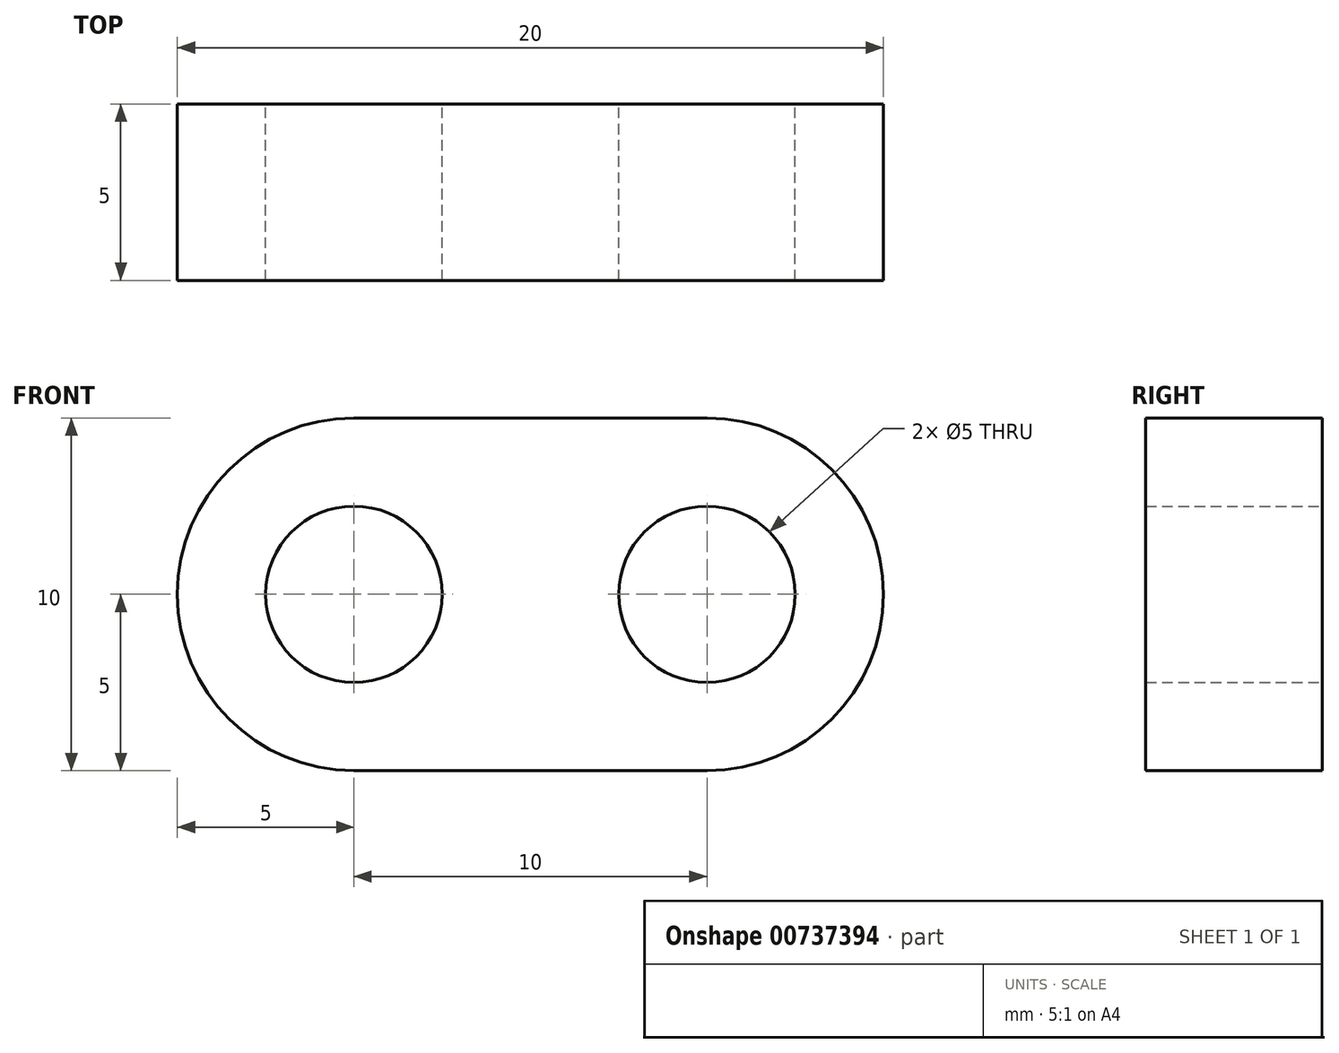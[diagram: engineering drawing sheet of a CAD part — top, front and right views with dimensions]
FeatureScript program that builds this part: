
annotation { "Feature Type Name" : "Feature", "Feature Type Description" : "" }
export const myFeature = defineFeature(function(context is Context, id is Id, definition is map)
    precondition{}
    {
        {
            var Q0;
            Q0=qCreatedBy(makeId("Front.planeOp"),FACE);
            var sketch = newSketch(context, id + "F0", { "sketchPlane" : qUnion([Q0])});
            skLineSegment(sketch, "E0.bottom", {"start": v(0, 0) * mm, "end": v(10, 0) * mm});
            skLineSegment(sketch, "E0.top", {"start": v(0, 10) * mm, "end": v(10, 10) * mm});
            skArc(sketch, "E1", {"start": v(10, 0) * mm, "mid": v(15, 5) * mm, "end": v(10, 10) * mm});
            skArc(sketch, "E2", {"start": v(0, 10) * mm, "mid": v(-5, 5) * mm, "end": v(0, 0) * mm});
            skCircle(sketch, "E3", {"center": v(0, 5) * mm, "radius": 2.5 * mm});
            skCircle(sketch, "E4", {"center": v(10, 5) * mm, "radius": 2.5 * mm});
            skSolve(sketch);
        }
        {
            var Q0;
            Q0=makeQuery(id+"F0.imprint","IMPRINT",FACE,{"disambiguationData":[TD([[makeQuery(id+"F0.imprint","IMPRINT",EDGE,{"derivedFrom":sQuery(id+"F0.wireOp",EDGE,"E0.bottom")}),1.0]])]});
            var Q1;
            Q1=makeQuery(id+"F0.imprint","IMPRINT",FACE,{"disambiguationData":[TD([[makeQuery(id+"F0.imprint","IMPRINT",EDGE,{"derivedFrom":sQuery(id+"F0.wireOp",EDGE,"oxad4vhf-pd54-7uuk-ZnQR-99PdKl2qKgE8")}),1.0]])]});
            var Q2;
            Q2=makeQuery(id+"F0.imprint","IMPRINT",FACE,{"disambiguationData":[TD([[makeQuery(id+"F0.imprint","IMPRINT",EDGE,{"derivedFrom":sQuery(id+"F0.wireOp",EDGE,"p5xoTqFS-tro0-XjQH-eI7p-wU4K02YeJdpj")}),1.0]])]});
            extrude(context, id + "F1", {"entities" : qUnion([Q0, Q1, Q2]), "depth" : 5 * mm, "offsetDistance" : 25 * mm});
        }
    });
